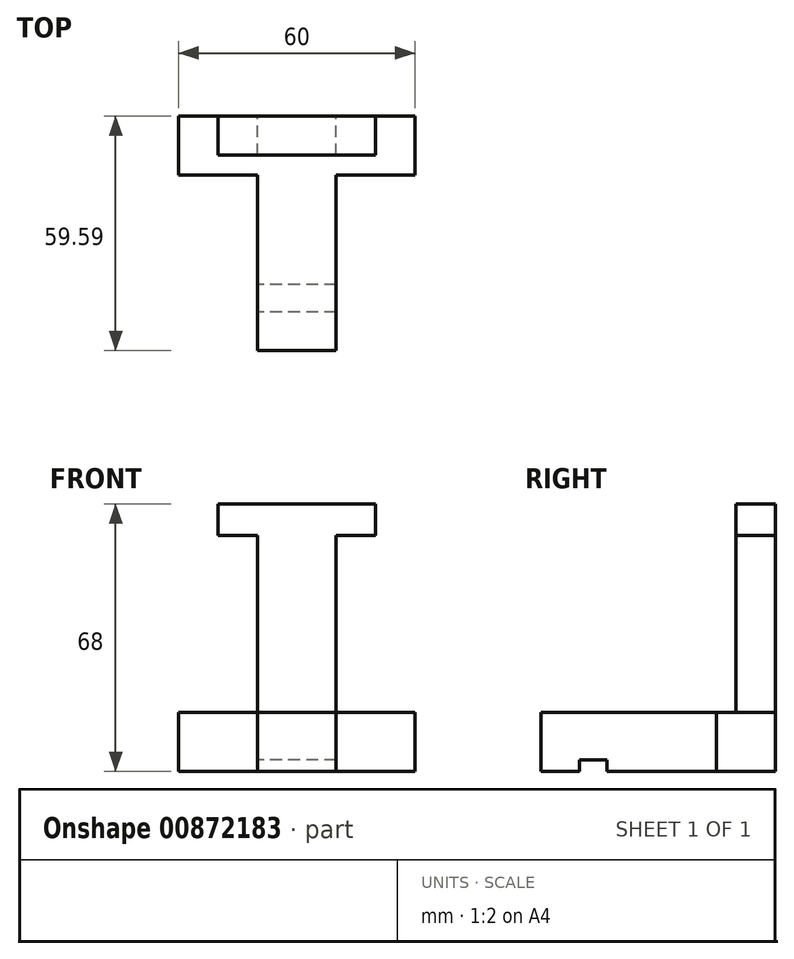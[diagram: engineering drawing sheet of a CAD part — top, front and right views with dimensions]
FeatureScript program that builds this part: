
annotation { "Feature Type Name" : "Feature", "Feature Type Description" : "" }
export const myFeature = defineFeature(function(context is Context, id is Id, definition is map)
    precondition{}
    {
        {
            var Q0;
            Q0=qCreatedBy(makeId("Top.planeOp"),FACE);
            var sketch = newSketch(context, id + "F0", { "sketchPlane" : qUnion([Q0])});
            skLineSegment(sketch, "E0", {"start": v(0, 0) * mm, "end": v(-30, 0) * mm});
            skLineSegment(sketch, "E1", {"start": v(0, 0) * mm, "end": v(30, 0) * mm});
            skLineSegment(sketch, "E2", {"start": v(30, 0) * mm, "end": v(30, -15) * mm});
            skLineSegment(sketch, "E3", {"start": v(30, -15) * mm, "end": v(10, -15) * mm});
            skLineSegment(sketch, "E4", {"start": v(10, -15) * mm, "end": v(10, -59.6) * mm});
            skLineSegment(sketch, "E5", {"start": v(10, -59.6) * mm, "end": v(0, -59.6) * mm});
            skLineSegment(sketch, "E6", {"start": v(0, -59.6) * mm, "end": v(-10, -59.6) * mm});
            skLineSegment(sketch, "E7", {"start": v(-10, -59.6) * mm, "end": v(-10, -15) * mm});
            skLineSegment(sketch, "E8", {"start": v(-10, -15) * mm, "end": v(-30, -15) * mm});
            skLineSegment(sketch, "E9", {"start": v(-30, -15) * mm, "end": v(-30, 0) * mm});
            skSolve(sketch);
        }
        {
            var Q0;
            Q0=makeQuery(id+"F0.imprint","IMPRINT",FACE,{"disambiguationData":[TD([[makeQuery(id+"F0.imprint","IMPRINT",EDGE,{"derivedFrom":sQuery(id+"F0.wireOp",EDGE,"E0")}),1.0]])]});
            extrude(context, id + "F1", {"entities" : qUnion([Q0]), "depth" : 15 * mm, "offsetDistance" : 25 * mm});
        }
        {
            var Q0;
            Q0=makeQuery(id+"F1.opExtrude","CAP_FACE",FACE,{"disambiguationData":[OSD([sQuery(id+"F0.wireOp",EDGE,"E0"),sQuery(id+"F0.wireOp",EDGE,"E1"),sQuery(id+"F0.wireOp",EDGE,"E2"),sQuery(id+"F0.wireOp",EDGE,"E3"),sQuery(id+"F0.wireOp",EDGE,"E4"),sQuery(id+"F0.wireOp",EDGE,"E5"),sQuery(id+"F0.wireOp",EDGE,"E6"),sQuery(id+"F0.wireOp",EDGE,"E7"),sQuery(id+"F0.wireOp",EDGE,"E8"),sQuery(id+"F0.wireOp",EDGE,"E9")])],"isStart":true});
            var sketch = newSketch(context, id + "F2", { "sketchPlane" : qUnion([Q0])});
            skLineSegment(sketch, "E10.bottom", {"start": v(10, 42.79) * mm, "end": v(-10, 42.79) * mm});
            skLineSegment(sketch, "E10.top", {"start": v(10, 49.82) * mm, "end": v(-10, 49.82) * mm});
            skLineSegment(sketch, "E10.left", {"start": v(10, 42.79) * mm, "end": v(10, 49.82) * mm});
            skLineSegment(sketch, "E10.right", {"start": v(-10, 42.79) * mm, "end": v(-10, 49.82) * mm});
            skSolve(sketch);
        }
        {
            var Q0;
            Q0=makeQuery(id+"F2.imprint","IMPRINT",FACE,{"disambiguationData":[TD([[makeQuery(id+"F2.imprint","IMPRINT",EDGE,{"derivedFrom":sQuery(id+"F2.wireOp",EDGE,"E10.bottom")}),-1.0]])]});
            extrude(context, id + "F3", {"entities" : qUnion([Q0]), "operationType" : NewBodyOperationType.REMOVE, "oppositeDirection" : true, "depth" : 3 * mm, "offsetDistance" : 25 * mm});
        }
        {
            var Q0;
            Q0=qCreatedBy(makeId("Front.planeOp"),FACE);
            var sketch = newSketch(context, id + "F4", { "sketchPlane" : qUnion([Q0])});
            skLineSegment(sketch, "E11.bottom", {"start": v(0, 0) * mm, "end": v(0, 0) * mm});
            skLineSegment(sketch, "E11.top", {"start": v(0, 60) * mm, "end": v(0, 60) * mm});
            skLineSegment(sketch, "E11.left", {"start": v(0, 0) * mm, "end": v(0, 60) * mm});
            skLineSegment(sketch, "E11.right", {"start": v(0, 0) * mm, "end": v(0, 60) * mm, "construction": true});
            skLineSegment(sketch, "E12.bottom", {"start": v(0, 60) * mm, "end": v(20, 60) * mm});
            skLineSegment(sketch, "E12.top", {"start": v(0, 68) * mm, "end": v(20, 68) * mm});
            skLineSegment(sketch, "E12.left", {"start": v(0, 60) * mm, "end": v(0, 68) * mm});
            skLineSegment(sketch, "E12.right", {"start": v(20, 60) * mm, "end": v(20, 68) * mm});
            skLineSegment(sketch, "E13.bottom", {"start": v(0, 60) * mm, "end": v(-20, 60) * mm});
            skLineSegment(sketch, "E13.top", {"start": v(0, 68) * mm, "end": v(-20, 68) * mm});
            skLineSegment(sketch, "E13.right", {"start": v(-20, 60) * mm, "end": v(-20, 68) * mm});
            skLineSegment(sketch, "E14", {"start": v(-10, 60) * mm, "end": v(-10, 15) * mm});
            skLineSegment(sketch, "E15", {"start": v(10, 60) * mm, "end": v(10, 15.63) * mm});
            skLineSegment(sketch, "E16.bottom", {"start": v(-10, 15) * mm, "end": v(0, 15) * mm});
            skLineSegment(sketch, "E16.top", {"start": v(-10, 60) * mm, "end": v(0, 60) * mm});
            skLineSegment(sketch, "E16.left", {"start": v(-10, 15) * mm, "end": v(-10, 60) * mm});
            skLineSegment(sketch, "E16.right", {"start": v(0, 15) * mm, "end": v(0, 60) * mm});
            skLineSegment(sketch, "E17.bottom", {"start": v(0, 15) * mm, "end": v(10, 15) * mm});
            skLineSegment(sketch, "E17.top", {"start": v(0, 60) * mm, "end": v(10, 60) * mm});
            skLineSegment(sketch, "E17.right", {"start": v(10, 15) * mm, "end": v(10, 60) * mm});
            skLineSegment(sketch, "E18.bottom", {"start": v(-20, 60) * mm, "end": v(20, 60) * mm});
            skLineSegment(sketch, "E18.top", {"start": v(-20, 68) * mm, "end": v(20, 68) * mm});
            skSolve(sketch);
        }
        {
            var Q0;
            {var subQ0=sQuery(id+"F4.wireOp",EDGE,"E17.bottom");Q0=makeQuery(id+"F4.imprint","IMPRINT",FACE,{"disambiguationData":[TD([[makeQuery(id+"F4.imprint","IMPRINT",EDGE,{"derivedFrom":subQ0}),1.0]])]});}
            var Q1;
            Q1=makeQuery(id+"F4.imprint","IMPRINT",FACE,{"disambiguationData":[TD([[makeQuery(id+"F4.imprint","IMPRINT",EDGE,{"derivedFrom":sQuery(id+"F4.wireOp",EDGE,"E16.bottom")}),1.0]])]});
            var Q2;
            {var subQ1=sQuery(id+"F4.wireOp",EDGE,"E12.left");Q2=makeQuery(id+"F4.imprint","IMPRINT",FACE,{"disambiguationData":[TD([[makeQuery(id+"F4.imprint","IMPRINT",EDGE,{"derivedFrom":subQ1}),1.0]])]});}
            var Q3;
            {var subQ1=sQuery(id+"F4.wireOp",EDGE,"E12.left");Q3=makeQuery(id+"F4.imprint","IMPRINT",FACE,{"disambiguationData":[TD([[makeQuery(id+"F4.imprint","IMPRINT",EDGE,{"derivedFrom":subQ1}),-1.0]])]});}
            extrude(context, id + "F5", {"entities" : qUnion([Q0, Q1, Q2, Q3]), "depth" : 10 * mm, "offsetDistance" : 25 * mm});
        }
    });
